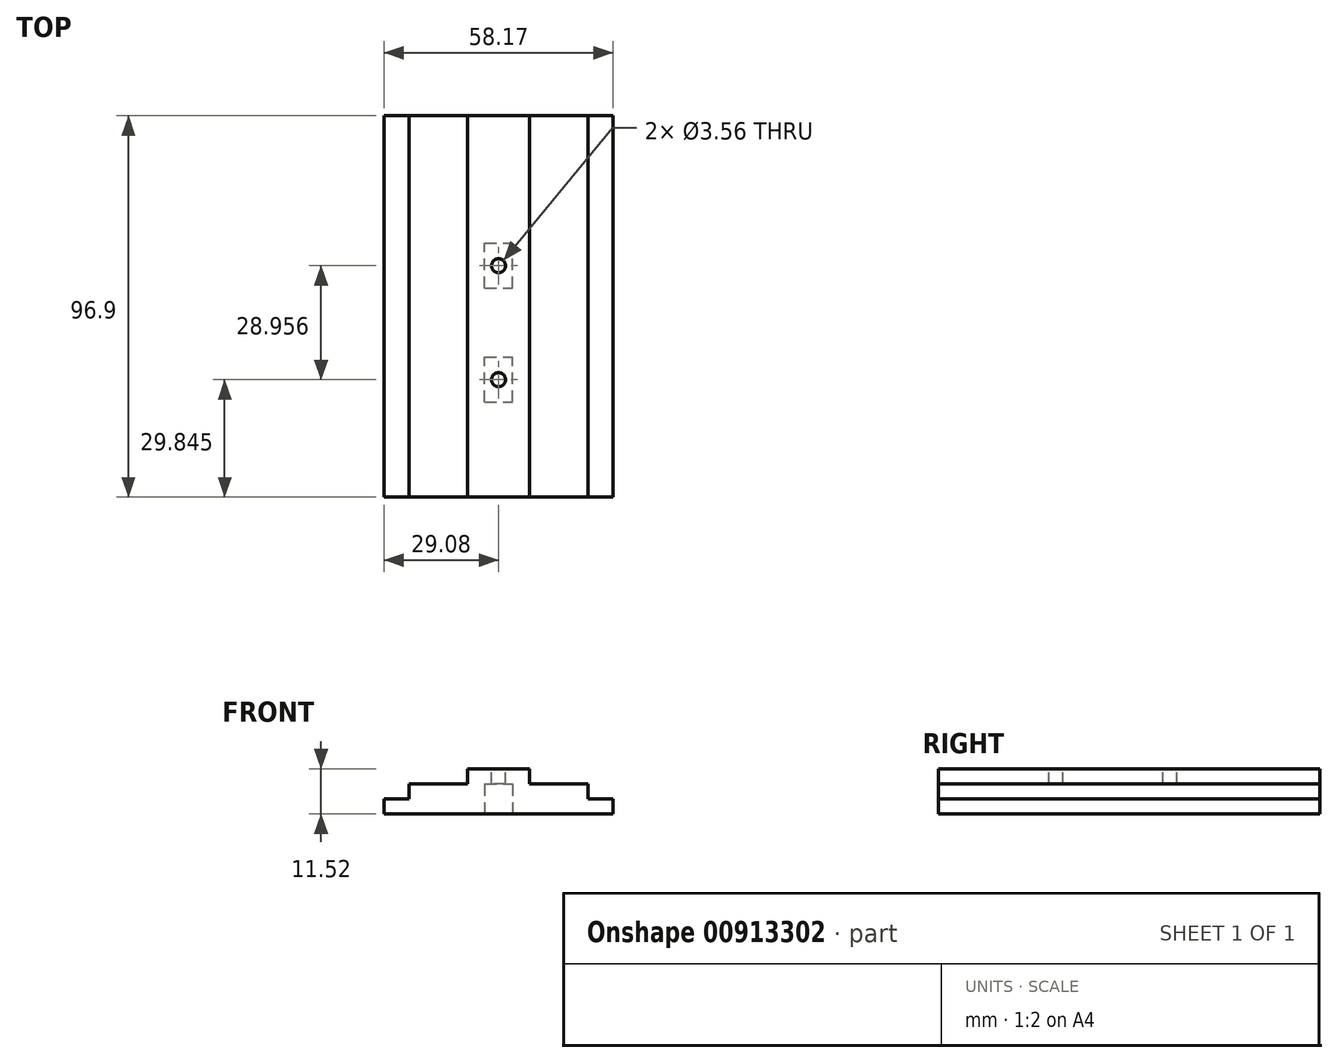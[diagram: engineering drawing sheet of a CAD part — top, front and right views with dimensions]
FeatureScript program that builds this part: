
annotation { "Feature Type Name" : "Feature", "Feature Type Description" : "" }
export const myFeature = defineFeature(function(context is Context, id is Id, definition is map)
    precondition{}
    {
        {
            var Q0;
            Q0=qCreatedBy(makeId("Front.planeOp"),FACE);
            var sketch = newSketch(context, id + "F0", { "sketchPlane" : qUnion([Q0])});
            skLineSegment(sketch, "E0", {"start": v(-29.08, -7.62) * mm, "end": v(29.09, -7.62) * mm});
            skLineSegment(sketch, "E1", {"start": v(29.09, -7.62) * mm, "end": v(29.09, -3.8) * mm});
            skLineSegment(sketch, "E2", {"start": v(29.09, -3.8) * mm, "end": v(22.74, -3.8) * mm});
            skLineSegment(sketch, "E3", {"start": v(22.74, -3.8) * mm, "end": v(22.74, 0) * mm});
            skLineSegment(sketch, "E4", {"start": v(22.74, 0) * mm, "end": v(7.83, 0) * mm});
            skLineSegment(sketch, "E5", {"start": v(7.83, 0) * mm, "end": v(7.83, 3.9) * mm});
            skLineSegment(sketch, "E6", {"start": v(7.83, 3.9) * mm, "end": v(-7.83, 3.9) * mm});
            skLineSegment(sketch, "E7", {"start": v(-7.83, 3.9) * mm, "end": v(-7.83, 0) * mm});
            skLineSegment(sketch, "E8", {"start": v(-7.83, 0) * mm, "end": v(-22.73, 0) * mm});
            skLineSegment(sketch, "E9", {"start": v(-22.73, 0) * mm, "end": v(-22.73, -3.81) * mm});
            skLineSegment(sketch, "E10", {"start": v(-22.73, -3.81) * mm, "end": v(-29.08, -3.81) * mm});
            skLineSegment(sketch, "E11", {"start": v(-29.08, -3.81) * mm, "end": v(-29.08, -7.62) * mm});
            skPoint(sketch, "E12", {"position": v(0, 3.9) * mm});
            skSolve(sketch);
        }
        {
            var Q0;
            Q0=makeQuery(id+"F0.imprint","IMPRINT",FACE,{"disambiguationData":[TD([[makeQuery(id+"F0.imprint","IMPRINT",EDGE,{"derivedFrom":sQuery(id+"F0.wireOp",EDGE,"E0")}),1.0]])]});
            extrude(context, id + "F1", {"entities" : qUnion([Q0]), "endBound" : BoundingType.SYMMETRIC, "depth" : 96.9 * mm, "offsetDistance" : 25.4 * mm});
        }
        {
            var Q0;
            Q0=makeQuery(id+"F1.opExtrude","SWEPT_FACE",FACE,{"disambiguationData":[OSD([sQuery(id+"F0.wireOp",EDGE,"E6")])]});
            var sketch = newSketch(context, id + "F2", { "sketchPlane" : qUnion([Q0])});
            skCircle(sketch, "E13", {"center": v(0, 10.35) * mm, "radius": 1.78 * mm});
            skCircle(sketch, "E14", {"center": v(0, -18.6) * mm, "radius": 1.78 * mm});
            skSolve(sketch);
        }
        {
            var Q0;
            Q0=makeQuery(id+"F2.imprint","IMPRINT",FACE,{"disambiguationData":[TD([[makeQuery(id+"F2.imprint","IMPRINT",EDGE,{"derivedFrom":sQuery(id+"F2.wireOp",EDGE,"E13")}),1.0]])]});
            var Q1;
            Q1=makeQuery(id+"F2.imprint","IMPRINT",FACE,{"disambiguationData":[TD([[makeQuery(id+"F2.imprint","IMPRINT",EDGE,{"derivedFrom":sQuery(id+"F2.wireOp",EDGE,"E14")}),1.0]])]});
            extrude(context, id + "F3", {"entities" : qUnion([Q0, Q1]), "operationType" : NewBodyOperationType.REMOVE, "endBound" : BoundingType.THROUGH_ALL, "oppositeDirection" : true, "depth" : 25.4 * mm, "offsetDistance" : 25.4 * mm});
        }
        {
            var Q0;
            Q0=makeQuery(id+"F1.opExtrude","SWEPT_FACE",FACE,{"disambiguationData":[OSD([sQuery(id+"F0.wireOp",EDGE,"E0")])]});
            var sketch = newSketch(context, id + "F4", { "sketchPlane" : qUnion([Q0])});
            skLineSegment(sketch, "E15.bottom", {"start": v(-3.5, 24.32) * mm, "end": v(3.5, 24.32) * mm});
            skLineSegment(sketch, "E15.top", {"start": v(-3.5, 12.9) * mm, "end": v(3.5, 12.9) * mm});
            skLineSegment(sketch, "E15.left", {"start": v(-3.5, 24.32) * mm, "end": v(-3.5, 12.9) * mm});
            skLineSegment(sketch, "E15.right", {"start": v(3.5, 24.32) * mm, "end": v(3.5, 12.9) * mm});
            skLineSegment(sketch, "E16.bottom", {"start": v(-3.5, -4.64) * mm, "end": v(3.5, -4.64) * mm});
            skLineSegment(sketch, "E16.top", {"start": v(-3.5, -16.07) * mm, "end": v(3.5, -16.07) * mm});
            skLineSegment(sketch, "E16.left", {"start": v(-3.5, -4.64) * mm, "end": v(-3.5, -16.07) * mm});
            skLineSegment(sketch, "E16.right", {"start": v(3.5, -4.64) * mm, "end": v(3.5, -16.07) * mm});
            skPoint(sketch, "E17", {"position": v(0, 18.6) * mm});
            skPoint(sketch, "E18", {"position": v(3.5, -10.35) * mm});
            skPoint(sketch, "E19", {"position": v(0, -4.64) * mm});
            skPoint(sketch, "E20", {"position": v(0, 24.32) * mm});
            skPoint(sketch, "E21", {"position": v(-3.5, 18.6) * mm});
            skPoint(sketch, "E22", {"position": v(0, -10.35) * mm});
            skSolve(sketch);
        }
        {
            var Q0;
            Q0=makeQuery(id+"F4.imprint","IMPRINT",FACE,{"disambiguationData":[TD([[makeQuery(id+"F4.imprint","IMPRINT",EDGE,{"derivedFrom":sQuery(id+"F4.wireOp",EDGE,"E15.bottom")}),-1.0]])]});
            var Q1;
            Q1=makeQuery(id+"F4.imprint","IMPRINT",FACE,{"disambiguationData":[TD([[makeQuery(id+"F4.imprint","IMPRINT",EDGE,{"derivedFrom":sQuery(id+"F4.wireOp",EDGE,"E16.bottom")}),-1.0]])]});
            var Q2;
            Q2=qCreatedBy(makeId("Top.planeOp"),FACE);
            extrude(context, id + "F5", {"entities" : qUnion([Q0, Q1]), "operationType" : NewBodyOperationType.REMOVE, "endBound" : BoundingType.UP_TO_SURFACE, "oppositeDirection" : true, "depth" : 25.4 * mm, "endBoundEntityFace" : qUnion([Q2]), "offsetDistance" : 25.4 * mm});
        }
    });
